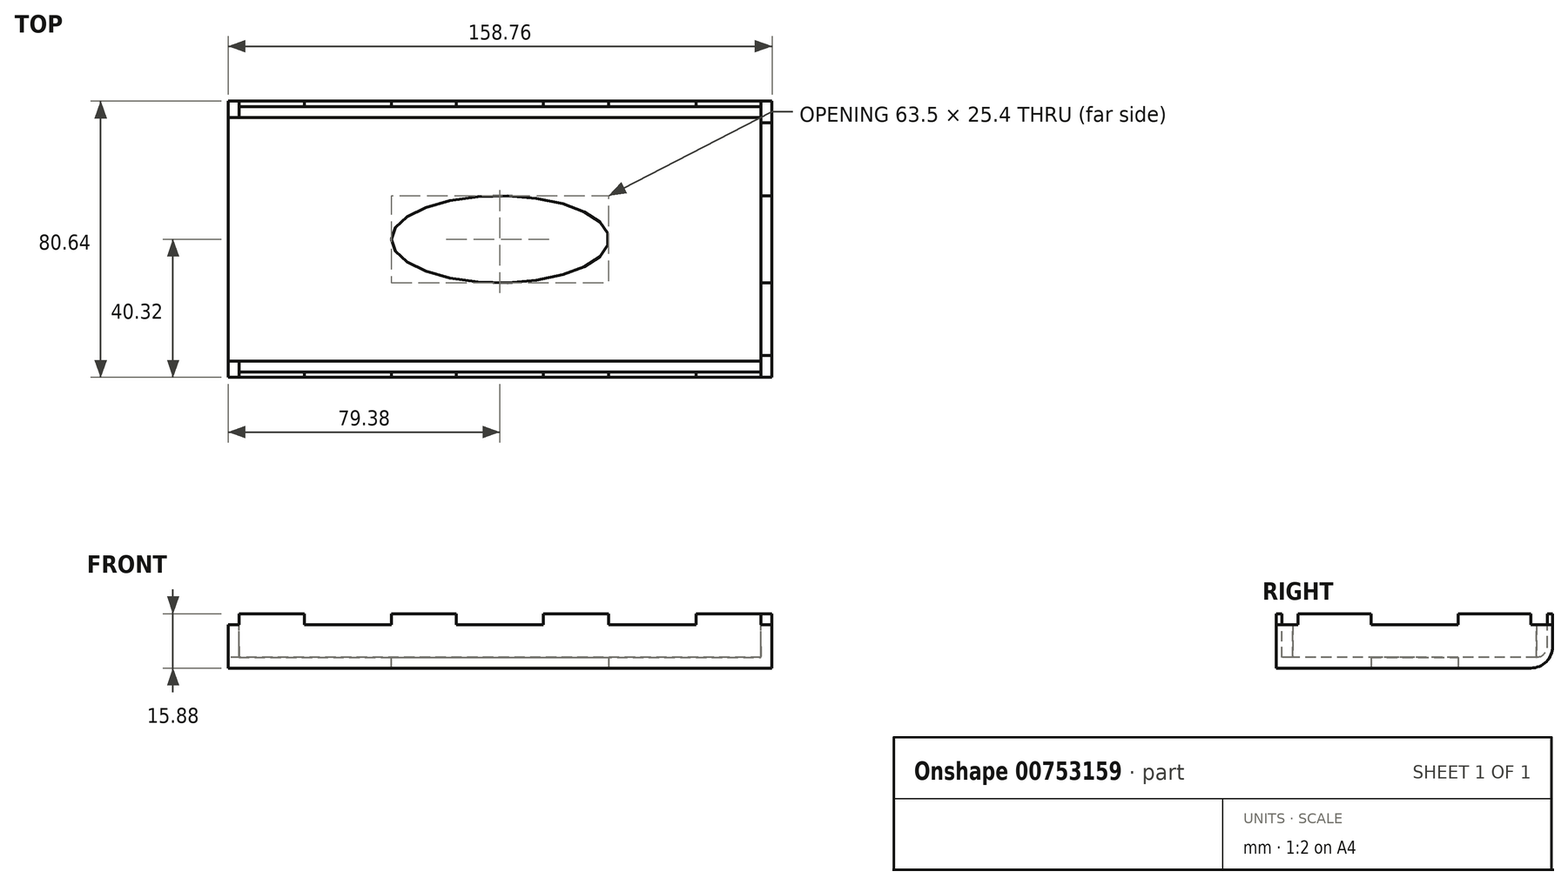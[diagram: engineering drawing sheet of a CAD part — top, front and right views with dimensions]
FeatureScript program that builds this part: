
annotation { "Feature Type Name" : "Feature", "Feature Type Description" : "" }
export const myFeature = defineFeature(function(context is Context, id is Id, definition is map)
    precondition{}
    {
        {
            var Q0;
            Q0=qCreatedBy(makeId("Top.planeOp"),FACE);
            var sketch = newSketch(context, id + "F0", { "sketchPlane" : qUnion([Q0])});
            skLineSegment(sketch, "E0.bottom", {"start": v(79.38, 40.32) * mm, "end": v(-79.38, 40.32) * mm});
            skLineSegment(sketch, "E0.top", {"start": v(79.38, -40.32) * mm, "end": v(-79.38, -40.32) * mm});
            skLineSegment(sketch, "E0.left", {"start": v(79.38, 40.32) * mm, "end": v(79.38, -40.32) * mm});
            skLineSegment(sketch, "E0.right", {"start": v(-79.38, 40.32) * mm, "end": v(-79.38, -40.32) * mm});
            skPoint(sketch, "E0.middle", {"position": v(0, 0) * mm});
            skSolve(sketch);
        }
        {
            var Q0;
            Q0 = qSketchRegion(id + "F0", true);
            extrude(context, id + "F1", {"entities" : qUnion([Q0]), "depth" : 15.88 * mm, "offsetDistance" : 25.4 * mm});
        }
        {
            var Q0;
            Q0=makeQuery(id+"F1.opExtrude","SWEPT_FACE",FACE,{"disambiguationData":[OSD([sQuery(id+"F0.wireOp",EDGE,"E0.right")])]});
            var sketch = newSketch(context, id + "F2", { "sketchPlane" : qUnion([Q0])});
            skLineSegment(sketch, "E1.bottom", {"start": v(-35.56, 12.76) * mm, "end": v(35.56, 12.76) * mm});
            skLineSegment(sketch, "E1.top", {"start": v(-35.56, 3.11) * mm, "end": v(35.56, 3.11) * mm});
            skLineSegment(sketch, "E1.left", {"start": v(-35.56, 12.76) * mm, "end": v(-35.56, 3.11) * mm});
            skLineSegment(sketch, "E1.right", {"start": v(35.56, 12.76) * mm, "end": v(35.56, 3.11) * mm});
            skPoint(sketch, "E1.middle", {"position": v(0, 7.94) * mm});
            skPoint(sketch, "E1.middle.positionSnap0", {"position": v(-40.32, 7.94) * mm});
            skPoint(sketch, "E1.centerSnap0", {"position": v(-40.32, 7.94) * mm});
            skSolve(sketch);
        }
        {
            var Q0;
            Q0 = qSketchRegion(id + "F2", true);
            extrude(context, id + "F3", {"entities" : qUnion([Q0]), "operationType" : NewBodyOperationType.REMOVE, "oppositeDirection" : true, "depth" : 155.57 * mm, "offsetDistance" : 25.4 * mm});
        }
        {
            var Q0;
            Q0=makeQuery(id+"F1.opExtrude","CAP_FACE",FACE,{"disambiguationData":[OSD([sQuery(id+"F0.wireOp",EDGE,"E0.bottom"),sQuery(id+"F0.wireOp",EDGE,"E0.top"),sQuery(id+"F0.wireOp",EDGE,"E0.left"),sQuery(id+"F0.wireOp",EDGE,"E0.right")])],"isStart":false});
            var sketch = newSketch(context, id + "F4", { "sketchPlane" : qUnion([Q0])});
            skLineSegment(sketch, "E2", {"start": v(-79.38, 0) * mm, "end": v(-76.2, 0) * mm});
            skLineSegment(sketch, "E3.bottom", {"start": v(-76.2, 38.74) * mm, "end": v(76.2, 38.73) * mm});
            skLineSegment(sketch, "E3.top", {"start": v(-76.2, -38.73) * mm, "end": v(76.2, -38.74) * mm});
            skLineSegment(sketch, "E3.left", {"start": v(-76.2, 38.74) * mm, "end": v(-76.2, -38.73) * mm});
            skLineSegment(sketch, "E3.right", {"start": v(76.2, 38.73) * mm, "end": v(76.2, -38.74) * mm});
            skPoint(sketch, "E3.middle", {"position": v(0, 0) * mm});
            skSolve(sketch);
        }
        {
            var Q0;
            Q0 = qSketchRegion(id + "F4", true);
            extrude(context, id + "F5", {"entities" : qUnion([Q0]), "operationType" : NewBodyOperationType.REMOVE, "oppositeDirection" : true, "depth" : 12.7 * mm, "offsetDistance" : 25.4 * mm});
        }
        {
            var Q0;
            Q0=makeQuery(id+"F1.opExtrude","CAP_FACE",FACE,{"disambiguationData":[OSD([sQuery(id+"F0.wireOp",EDGE,"E0.bottom"),sQuery(id+"F0.wireOp",EDGE,"E0.top"),sQuery(id+"F0.wireOp",EDGE,"E0.left"),sQuery(id+"F0.wireOp",EDGE,"E0.right")])],"isStart":false});
            var sketch = newSketch(context, id + "F6", { "sketchPlane" : qUnion([Q0])});
            skLineSegment(sketch, "E4.bottom", {"start": v(-76.2, -40.32) * mm, "end": v(-79.38, -40.32) * mm});
            skLineSegment(sketch, "E4.top", {"start": v(-76.2, 0) * mm, "end": v(-79.38, 0) * mm});
            skLineSegment(sketch, "E4.left", {"start": v(-76.2, -40.32) * mm, "end": v(-76.2, 0) * mm});
            skLineSegment(sketch, "E4.right", {"start": v(-79.38, -40.32) * mm, "end": v(-79.38, 0) * mm});
            skPoint(sketch, "E5.middle", {"position": v(-77.79, 0) * mm});
            skPoint(sketch, "E5.middle.positionSnap0", {"position": v(-77.79, 0) * mm});
            skPoint(sketch, "E5.centerSnap0", {"position": v(-77.79, 0) * mm});
            skLineSegment(sketch, "E6.bottom", {"start": v(-57.15, -40.32) * mm, "end": v(-31.75, -40.32) * mm});
            skLineSegment(sketch, "E6.top", {"start": v(-57.15, -38.74) * mm, "end": v(-31.75, -38.74) * mm});
            skLineSegment(sketch, "E6.left", {"start": v(-57.15, -40.32) * mm, "end": v(-57.15, -38.74) * mm});
            skLineSegment(sketch, "E6.right", {"start": v(-31.75, -40.32) * mm, "end": v(-31.75, -38.74) * mm});
            skLineSegment(sketch, "E7.bottom", {"start": v(-12.7, -40.32) * mm, "end": v(12.7, -40.32) * mm});
            skLineSegment(sketch, "E7.top", {"start": v(-12.7, -38.74) * mm, "end": v(12.7, -38.74) * mm});
            skLineSegment(sketch, "E7.left", {"start": v(-12.7, -40.32) * mm, "end": v(-12.7, -38.74) * mm});
            skLineSegment(sketch, "E7.right", {"start": v(12.7, -40.32) * mm, "end": v(12.7, -38.74) * mm});
            skLineSegment(sketch, "E8.bottom", {"start": v(31.75, -40.32) * mm, "end": v(57.15, -40.32) * mm});
            skLineSegment(sketch, "E8.top", {"start": v(31.75, -38.74) * mm, "end": v(57.15, -38.74) * mm});
            skLineSegment(sketch, "E8.left", {"start": v(31.75, -40.32) * mm, "end": v(31.75, -38.74) * mm});
            skLineSegment(sketch, "E8.right", {"start": v(57.15, -40.32) * mm, "end": v(57.15, -38.74) * mm});
            skLineSegment(sketch, "E9.bottom", {"start": v(-79.38, 40.32) * mm, "end": v(-76.2, 40.32) * mm});
            skLineSegment(sketch, "E9.top", {"start": v(-79.38, 0) * mm, "end": v(-76.2, 0) * mm});
            skLineSegment(sketch, "E9.left", {"start": v(-79.38, 40.32) * mm, "end": v(-79.38, 0) * mm});
            skLineSegment(sketch, "E9.right", {"start": v(-76.2, 40.32) * mm, "end": v(-76.2, 0) * mm});
            skLineSegment(sketch, "E10.bottom", {"start": v(-57.15, 38.74) * mm, "end": v(-31.75, 38.74) * mm});
            skLineSegment(sketch, "E10.top", {"start": v(-57.15, 40.32) * mm, "end": v(-31.75, 40.32) * mm});
            skLineSegment(sketch, "E10.left", {"start": v(-57.15, 38.74) * mm, "end": v(-57.15, 40.32) * mm});
            skLineSegment(sketch, "E10.right", {"start": v(-31.75, 38.73) * mm, "end": v(-31.75, 40.32) * mm});
            skLineSegment(sketch, "E11.bottom", {"start": v(-12.7, 38.74) * mm, "end": v(12.7, 38.74) * mm});
            skLineSegment(sketch, "E11.top", {"start": v(-12.7, 40.32) * mm, "end": v(12.7, 40.32) * mm});
            skLineSegment(sketch, "E11.left", {"start": v(-12.7, 38.74) * mm, "end": v(-12.7, 40.32) * mm});
            skLineSegment(sketch, "E11.right", {"start": v(12.7, 38.73) * mm, "end": v(12.7, 40.32) * mm});
            skLineSegment(sketch, "E12.bottom", {"start": v(31.75, 40.32) * mm, "end": v(57.15, 40.32) * mm});
            skLineSegment(sketch, "E12.top", {"start": v(31.75, 38.73) * mm, "end": v(57.15, 38.73) * mm});
            skLineSegment(sketch, "E12.left", {"start": v(31.75, 40.32) * mm, "end": v(31.75, 38.73) * mm});
            skLineSegment(sketch, "E12.right", {"start": v(57.15, 40.32) * mm, "end": v(57.15, 38.73) * mm});
            skLineSegment(sketch, "E13.bottom", {"start": v(79.38, 40.32) * mm, "end": v(76.2, 40.32) * mm});
            skLineSegment(sketch, "E13.top", {"start": v(79.38, 33.97) * mm, "end": v(76.2, 33.97) * mm});
            skLineSegment(sketch, "E13.left", {"start": v(79.38, 40.32) * mm, "end": v(79.38, 33.97) * mm});
            skLineSegment(sketch, "E13.right", {"start": v(76.2, 40.32) * mm, "end": v(76.2, 33.97) * mm});
            skLineSegment(sketch, "E14.bottom", {"start": v(79.38, -40.32) * mm, "end": v(76.2, -40.32) * mm});
            skLineSegment(sketch, "E14.top", {"start": v(79.37, -33.97) * mm, "end": v(76.2, -33.97) * mm});
            skLineSegment(sketch, "E14.left", {"start": v(79.38, -40.32) * mm, "end": v(79.38, -33.97) * mm});
            skLineSegment(sketch, "E14.right", {"start": v(76.2, -40.32) * mm, "end": v(76.2, -33.97) * mm});
            skLineSegment(sketch, "E15.bottom", {"start": v(76.2, 12.7) * mm, "end": v(79.38, 12.7) * mm});
            skLineSegment(sketch, "E15.top", {"start": v(76.2, -12.7) * mm, "end": v(79.38, -12.7) * mm});
            skLineSegment(sketch, "E15.left", {"start": v(76.2, 12.7) * mm, "end": v(76.2, -12.7) * mm});
            skLineSegment(sketch, "E15.right", {"start": v(79.38, 12.7) * mm, "end": v(79.38, -12.7) * mm});
            skSolve(sketch);
        }
        {
            var Q0;
            Q0 = qSketchRegion(id + "F6", true);
            extrude(context, id + "F7", {"entities" : qUnion([Q0]), "operationType" : NewBodyOperationType.REMOVE, "oppositeDirection" : true, "depth" : 3.17 * mm, "offsetDistance" : 25.4 * mm});
        }
        {
            var Q0;
            Q0=makeQuery(id+"F3.boolean.opBoolean","COPY",FACE,{"derivedFrom":makeQuery(id+"F3.opExtrude","SWEPT_FACE",FACE,{"disambiguationData":[OSD([sQuery(id+"F2.wireOp",EDGE,"E1.top")])]})});
            var sketch = newSketch(context, id + "F8", { "sketchPlane" : qUnion([Q0])});
            skEllipse(sketch, "E16", {"center": v(0, 0) * mm, "majorRadius": 31.75 * mm, "minorRadius": 12.7 * mm, "majorAxis": v(-1, 0)});
            skSolve(sketch);
        }
        {
            var Q0;
            Q0 = qSketchRegion(id + "F8", true);
            extrude(context, id + "F9", {"entities" : qUnion([Q0]), "operationType" : NewBodyOperationType.REMOVE, "oppositeDirection" : true, "depth" : 25.4 * mm, "offsetDistance" : 25.4 * mm});
        }
        {
            var Q0;
            Q0=makeQuery(id+"F5.boolean.opBoolean","COPY",EDGE,{"derivedFrom":makeQuery(id+"F5.opExtrude","CAP_EDGE",EDGE,{"disambiguationData":[OSD([sQuery(id+"F4.wireOp",EDGE,"E3.bottom")])],"isStart":false})});
            fillet(context, id + "F10", {"entities" : qUnion([Q0]), "radius" : 3.17 * mm, "tangentPropagation" : true, "allowEdgeOverflow" : false});
        }
        {
            var Q0;
            Q0=makeQuery(id+"F1.opExtrude","CAP_EDGE",EDGE,{"disambiguationData":[OSD([sQuery(id+"F0.wireOp",EDGE,"E0.bottom")])],"isStart":true});
            fillet(context, id + "F11", {"entities" : qUnion([Q0]), "radius" : 6.35 * mm, "tangentPropagation" : true, "allowEdgeOverflow" : false});
        }
    });
